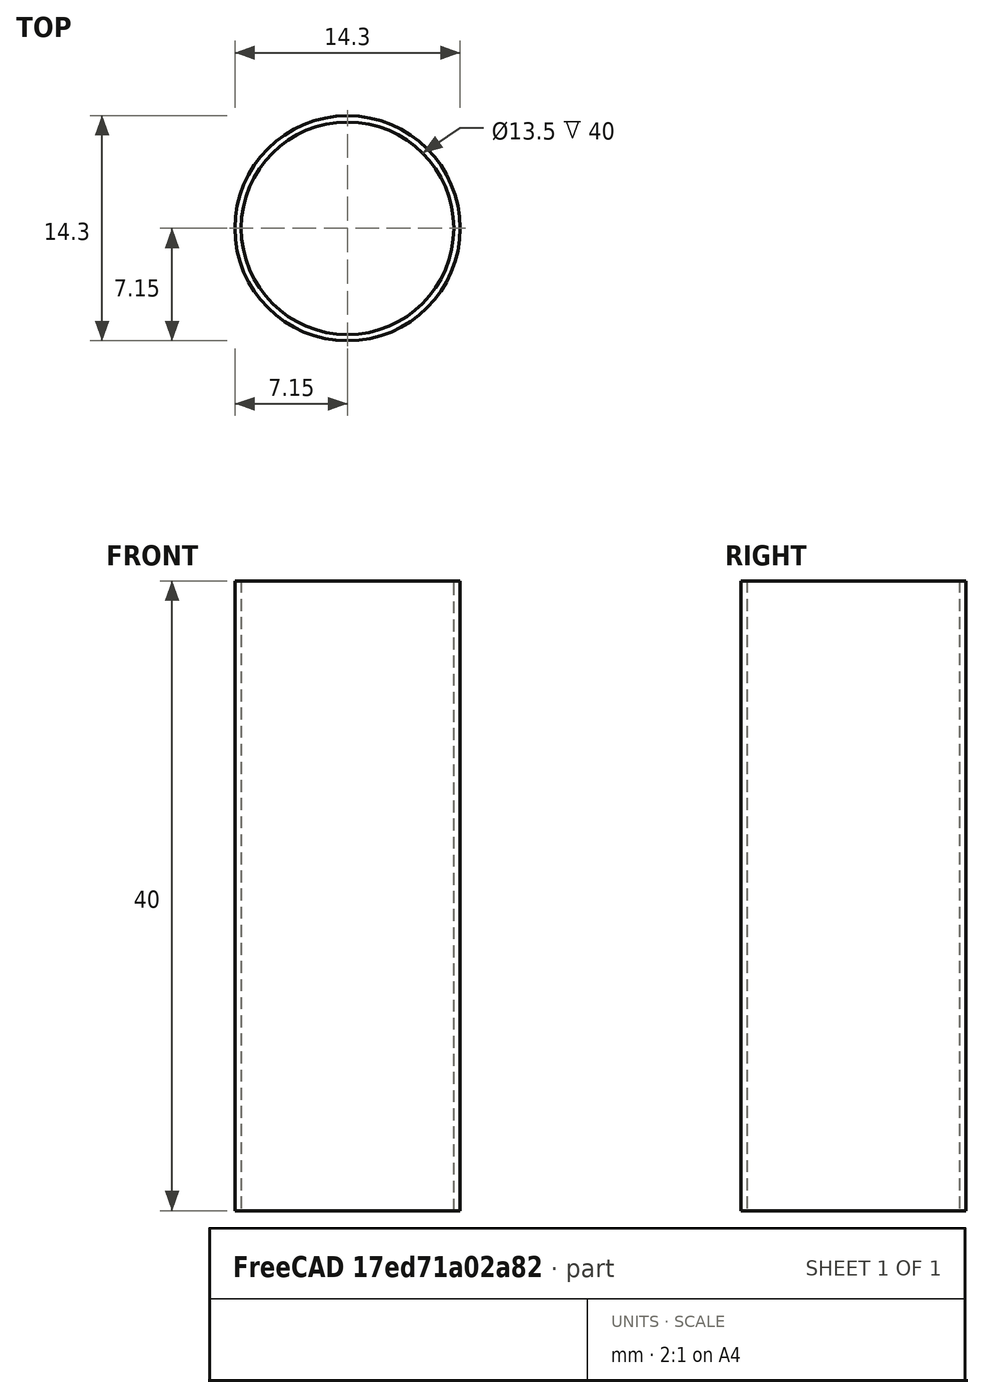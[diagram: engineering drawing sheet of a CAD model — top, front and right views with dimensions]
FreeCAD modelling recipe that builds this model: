
FCSTD DOCUMENT  (FreeCAD 0.19R23756 (Git))
Label: Tube
License: All rights reserved
LicenseURL: http://en.wikipedia.org/wiki/All_rights_reserved
objects: Sketcher::SketchObject×1, PartDesign::Pad×1, PartDesign::Body×1
note: 4 computed .brp shape members not serialized (recipe doc carries the construction recipe); baked Part::Feature solids carry a one-line shape summary decoded from their .brp

FEATURE [Sketcher::SketchObject] Sketch
  FullyConstrained = true
  MapMode = 5
  Support = -> [XY_Plane]
  sketch-geometry (2):
    g0: Circle CenterX=0 CenterY=0 CenterZ=0 NormalX=0 NormalY=0 NormalZ=1 AngleXU=0 Radius=6.75
    g1: Circle CenterX=0 CenterY=0 CenterZ=0 NormalX=0 NormalY=0 NormalZ=1 AngleXU=0 Radius=7.15
  constraints (4):
    c: Coincident(g0,g-1)
    c: Diameter(g0) = 13.5
    c: Coincident(g1,g0)
    c: Diameter(g1) = 14.3
FEATURE [PartDesign::Pad] Pad
  Direction = (1,1,1)
  Length = 40
  Length2 = 100
  Profile = -> Sketch
  Type = 0
FEATURE [PartDesign::Body] Body
  Group = -> [Sketch,Pad]
  Origin = -> Origin
  Tip = -> Pad
